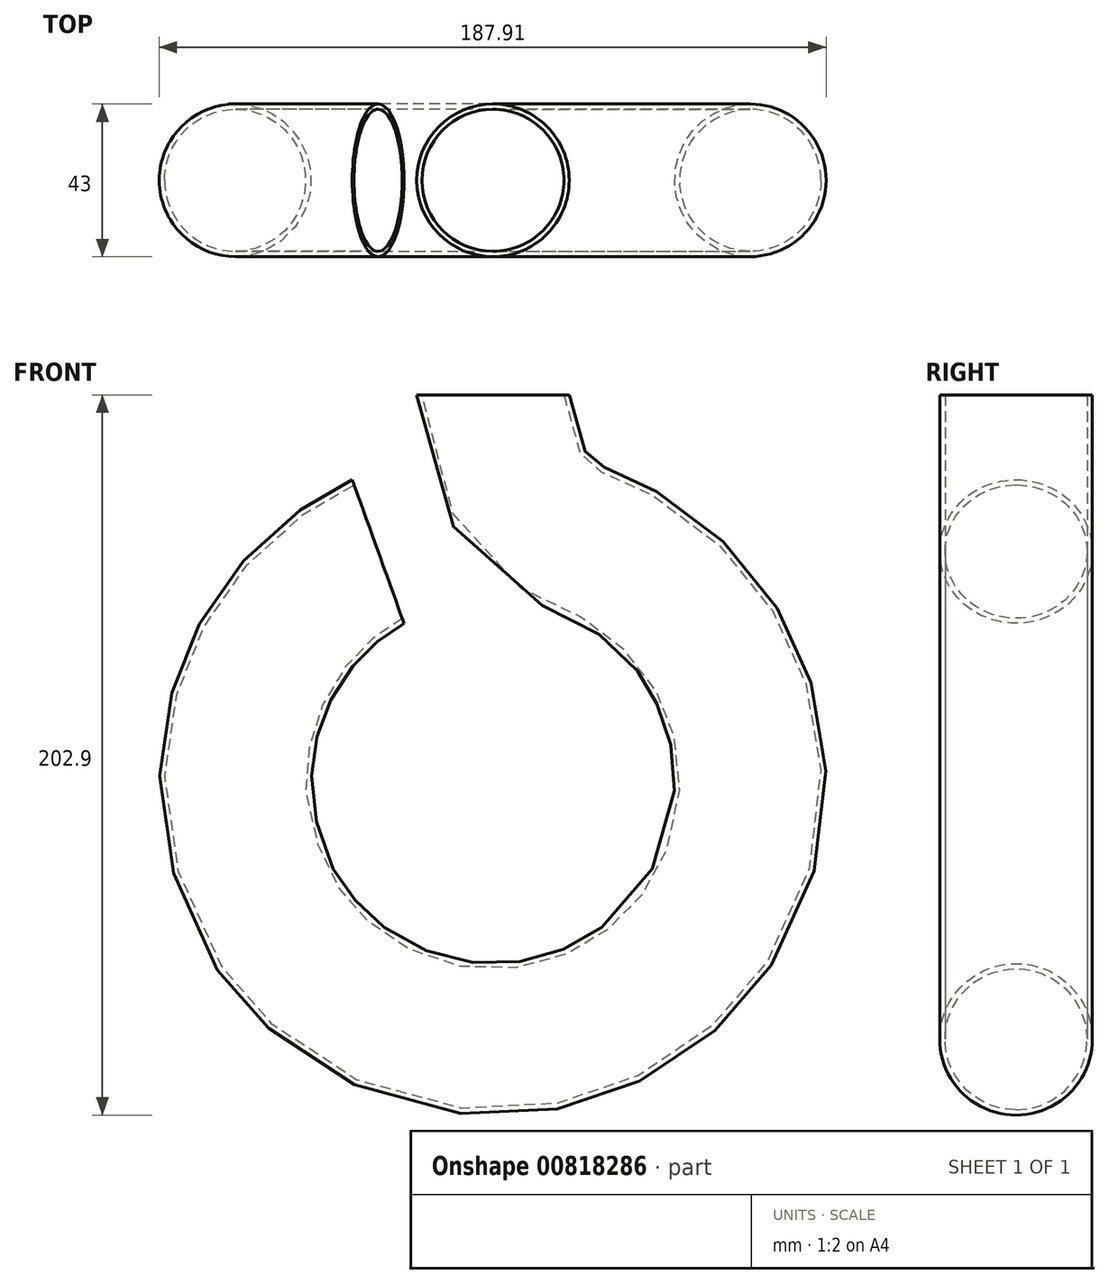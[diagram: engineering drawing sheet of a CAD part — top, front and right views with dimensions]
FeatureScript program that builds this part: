
annotation { "Feature Type Name" : "Feature", "Feature Type Description" : "" }
export const myFeature = defineFeature(function(context is Context, id is Id, definition is map)
    precondition{}
    {
        {
            var Q0;
            Q0=qCreatedBy(makeId("Top.planeOp"),FACE);
            var sketch = newSketch(context, id + "F0", { "sketchPlane" : qUnion([Q0])});
            skCircle(sketch, "E0", {"center": v(0, 0) * mm, "radius": 21.5 * mm});
            skCircle(sketch, "E1", {"center": v(0, 0) * mm, "radius": 20 * mm});
            skSolve(sketch);
        }
        {
            var Q0;
            Q0=qCreatedBy(makeId("Front.planeOp"),FACE);
            var sketch = newSketch(context, id + "F1", { "sketchPlane" : qUnion([Q0])});
            skLineSegment(sketch, "E2.0.0", {"start": v(-20, 0) * mm, "end": v(20, 0) * mm, "construction": true});
            skLineSegment(sketch, "E3", {"start": v(0, 0) * mm, "end": v(0, -218) * mm, "construction": true});
            skLineSegment(sketch, "E4", {"start": v(0, -109) * mm, "end": v(109, -109) * mm, "construction": true});
            skLineSegment(sketch, "E5.MirrorCS", {"start": v(0, -109) * mm, "end": v(-109, -109) * mm, "construction": true});
            skCircle(sketch, "E6", {"center": v(0, -109) * mm, "radius": 72.5 * mm, "construction": true});
            skFitSpline(sketch, "E7", {"points": [v(0, 0) * mm, v(4.4, -19.56) * mm, v(13.05, -33.64) * mm, v(25.82, -41.25) * mm, v(34.92, -45.47) * mm, v(42.4, -50.2) * mm, v(55.27, -62.08) * mm, v(61.03, -69.86) * mm, v(66.74, -80.69) * mm, v(70.95, -94.07) * mm, v(72.5, -109) * mm, v(70, -127.86) * mm, v(62.21, -146.23) * mm, v(54.03, -157.34) * mm, v(44.23, -166.44) * mm, v(31.2, -174.45) * mm, v(18.83, -179.01) * mm, v(3.63, -181.4) * mm, v(-16.37, -179.63) * mm, v(-37.01, -171.34) * mm, v(-49.97, -161.53) * mm, v(-57.04, -153.76) * mm, v(-65.02, -141.08) * mm, v(-71.9, -118.38) * mm, v(-72.47, -106.88) * mm, v(-70.64, -92.67) * mm, v(-67.48, -82.5) * mm, v(-63.62, -74.24) * mm, v(-57.77, -65.2) * mm, v(-50.6, -57.08) * mm, v(-42.6, -50.33) * mm, v(-35.76, -45.93) * mm, v(-32.35, -44.12) * mm], "startDerivative": vector(64.07, -572.34) * mm, "endDerivative": vector(225.18, 110.78) * mm});
            skSolve(sketch);
        }
        {
            var Q0;
            Q0 = qSketchRegion(id + "F0", true);
            var Q1;
            Q1=sQuery(id+"F1.wireOp",EDGE,"E7");
            sweep(context, id + "F2", {"profiles" : qUnion([Q0]), "path" : qUnion([Q1])});
        }
    });
